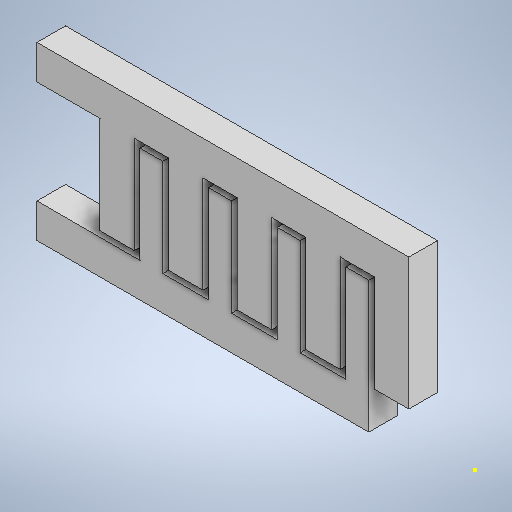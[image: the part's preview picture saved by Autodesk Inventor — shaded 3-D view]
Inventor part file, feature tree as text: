
AUTODESK INVENTOR PART (.ipt)
format: ipt  version: 2025.2 (Build 292293000, 293)  size: 308,736 bytes
history: native  units: mm
features: sketch x2, extrude x1
ambient origin geometry x8: Origin, YZ Plane, XZ Plane, XY Plane, X Axis, Y Axis, Z Axis, Center Point
bodies: Solid1 (feature_tree)
feature tree (3):
  sketch  "Sketch1"  dims[d90=6.0mm d91=6.0mm]
  sketch  "Sketch2"  dims[d92=5.0mm d93=0.0mm]
  extrude  "Extrusion1"  Depth=6.0mm
